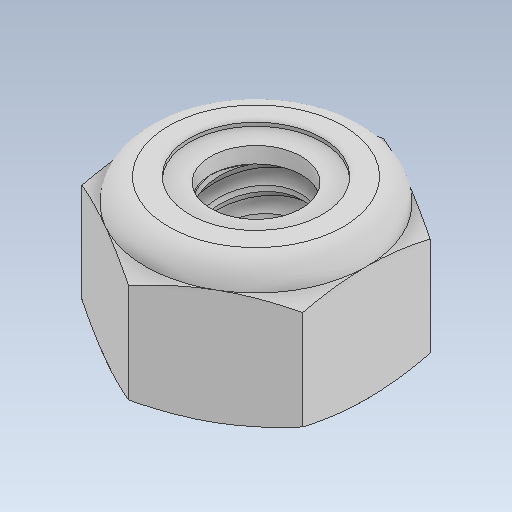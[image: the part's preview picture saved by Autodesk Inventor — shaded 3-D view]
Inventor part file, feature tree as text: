
AUTODESK INVENTOR PART (.ipt)
format: ipt  version: 2023 (Build 270158000, 158)  size: 274,432 bytes
history: native  units: in
note: dims shown in document units (in); Inventor stores cm internally (conversion verified against a paired STEP export)
features: other x1, revolve x1
ambient origin geometry x8: Origin, YZ Plane, XZ Plane, XY Plane, X Axis, Y Axis, Z Axis, Center Point
bodies: Solid1 (feature_tree), Solid2 (feature_tree)
feature tree (2):
  other  "Cut-Revolve4"
  revolve  "Revolve2"  [1 undecoded]
note: 1 required parameter value undecoded (feature->parameter linkage not recoverable at this tier; creation-order binding heuristic only, values carry confidence <= 0.55)
